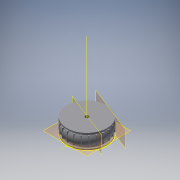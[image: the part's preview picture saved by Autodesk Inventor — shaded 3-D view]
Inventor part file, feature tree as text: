
AUTODESK INVENTOR PART (.ipt)
format: ipt  version: 2017 (Build 210142000, 142)  size: 517,632 bytes
history: native  units: mm
features: sketch x10, other x4, plane x4
ambient origin geometry x8: Origin, YZ Plane, XZ Plane, XY Plane, X Axis, Y Axis, Z Axis, Center Point
bodies: Solid1 (feature_tree)
feature tree (18):
  other  "front-wheel.ipt"
  other  "Solid1::front-wheel.ipt"
  other  "TaggingFeature1"
  sketch  "Sketch1"  dims[d0=10.0mm]
  sketch  "Sketch2"
  sketch  "Sketch3"
  sketch  "Sketch5"
  sketch  "Sketch6"
  sketch  "Sketch7"
  sketch  "Sketch8"
  sketch  "Sketch9"
  sketch  "Sketch11"
  sketch  "Sketch13"
  plane  "Work Plane1"
  plane  "Work Plane2"
  plane  "Work Plane3"
  plane  "Work Plane4"
  other  "Work Axis1"
